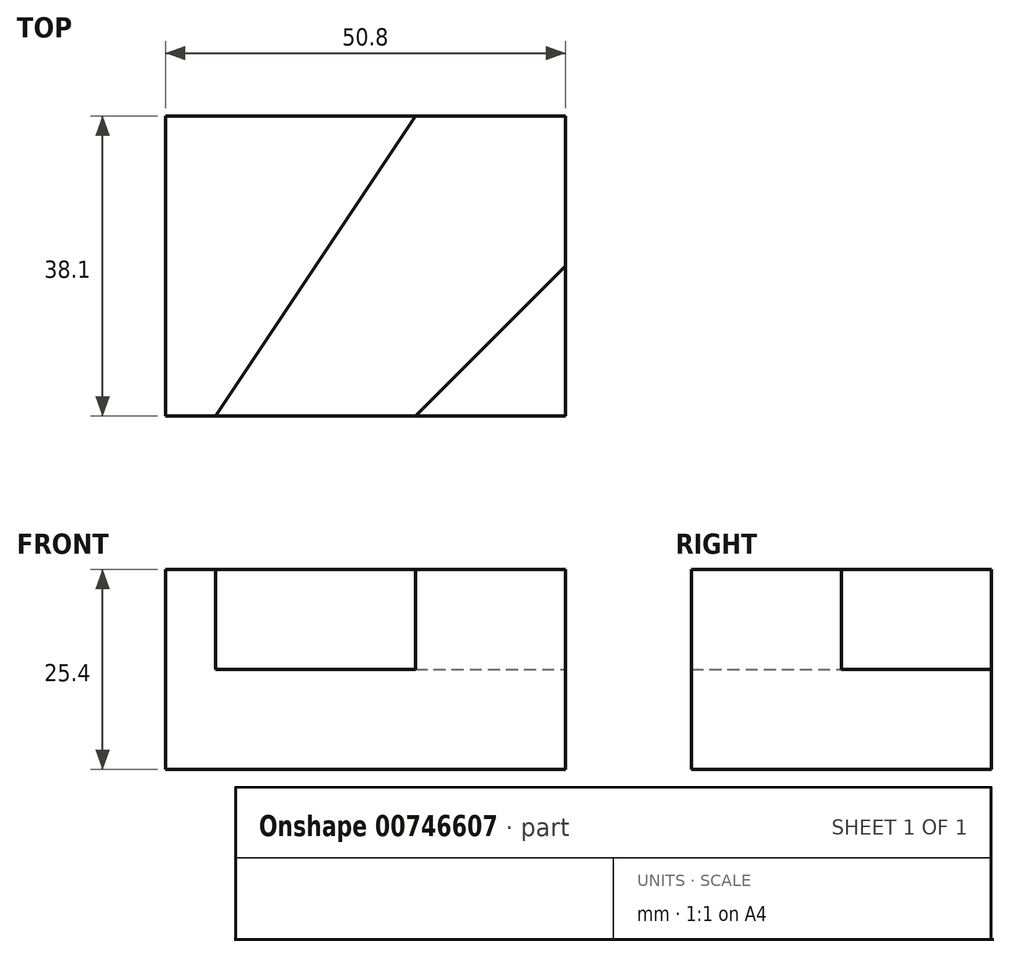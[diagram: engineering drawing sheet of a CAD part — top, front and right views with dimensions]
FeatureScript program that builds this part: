
annotation { "Feature Type Name" : "Feature", "Feature Type Description" : "" }
export const myFeature = defineFeature(function(context is Context, id is Id, definition is map)
    precondition{}
    {
        {
            var Q0;
            Q0=qCreatedBy(makeId("Front.planeOp"),FACE);
            var sketch = newSketch(context, id + "F0", { "sketchPlane" : qUnion([Q0])});
            skLineSegment(sketch, "E0.bottom", {"start": v(0, 0) * mm, "end": v(50.8, 0) * mm});
            skLineSegment(sketch, "E0.top", {"start": v(0, 25.4) * mm, "end": v(50.8, 25.4) * mm});
            skLineSegment(sketch, "E0.left", {"start": v(0, 0) * mm, "end": v(0, 25.4) * mm});
            skLineSegment(sketch, "E0.right", {"start": v(50.8, 0) * mm, "end": v(50.8, 25.4) * mm});
            skSolve(sketch);
        }
        {
            var Q0;
            Q0=makeQuery(id+"F0.imprint","IMPRINT",FACE,{"disambiguationData":[TD([[makeQuery(id+"F0.imprint","IMPRINT",EDGE,{"derivedFrom":sQuery(id+"F0.wireOp",EDGE,"E0.bottom")}),1.0]])]});
            extrude(context, id + "F1", {"entities" : qUnion([Q0]), "oppositeDirection" : true, "depth" : 38.1 * mm, "offsetDistance" : 25.4 * mm});
        }
        {
            var Q0;
            Q0=makeQuery(id+"F1.opExtrude","SWEPT_FACE",FACE,{"disambiguationData":[OSD([sQuery(id+"F0.wireOp",EDGE,"E0.top")])]});
            var sketch = newSketch(context, id + "F2", { "sketchPlane" : qUnion([Q0])});
            skLineSegment(sketch, "E1", {"start": v(6.35, 0) * mm, "end": v(31.75, 38.1) * mm});
            skLineSegment(sketch, "E2", {"start": v(31.75, 38.1) * mm, "end": v(50.8, 38.1) * mm});
            skLineSegment(sketch, "E3", {"start": v(50.8, 38.1) * mm, "end": v(50.8, 19.05) * mm});
            skLineSegment(sketch, "E4", {"start": v(50.8, 19.05) * mm, "end": v(31.75, 0) * mm});
            skLineSegment(sketch, "E5", {"start": v(31.75, 0) * mm, "end": v(6.35, 0) * mm});
            skLineSegment(sketch, "E6", {"start": v(6.35, 0) * mm, "end": v(0, 0) * mm});
            skSolve(sketch);
        }
        {
            var Q0;
            Q0=makeQuery(id+"F2.imprint","IMPRINT",FACE,{"disambiguationData":[TD([[makeQuery(id+"F2.imprint","IMPRINT",EDGE,{"derivedFrom":sQuery(id+"F2.wireOp",EDGE,"E1")}),-1.0]])]});
            extrude(context, id + "F3", {"entities" : qUnion([Q0]), "operationType" : NewBodyOperationType.REMOVE, "oppositeDirection" : true, "depth" : 12.7 * mm, "offsetDistance" : 25.4 * mm});
        }
    });
